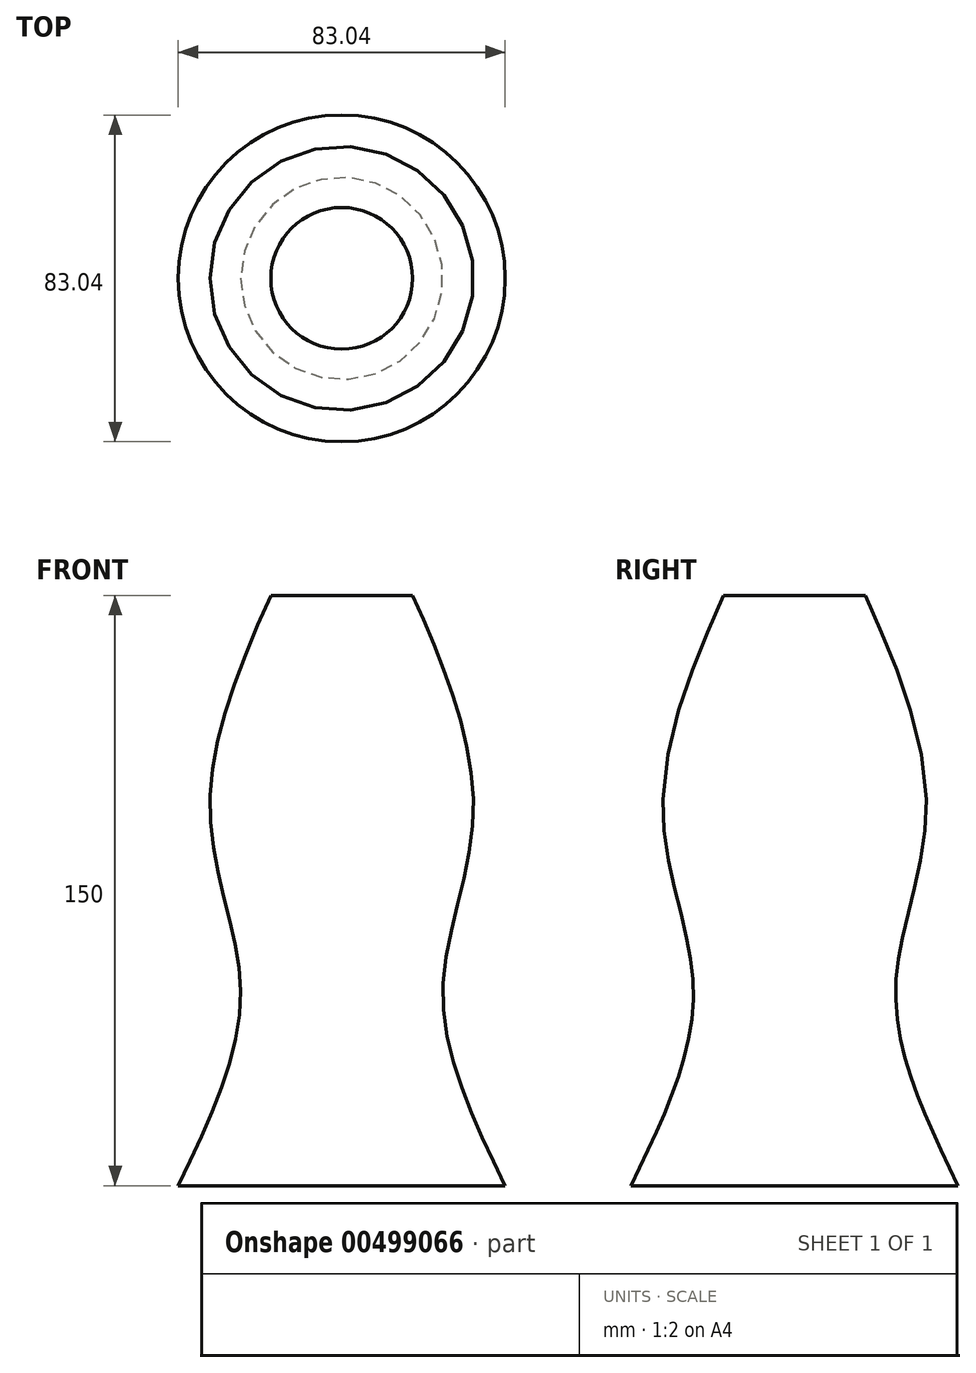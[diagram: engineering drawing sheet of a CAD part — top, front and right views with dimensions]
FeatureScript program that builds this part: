
annotation { "Feature Type Name" : "Feature", "Feature Type Description" : "" }
export const myFeature = defineFeature(function(context is Context, id is Id, definition is map)
    precondition{}
    {
        {
            var Q0;
            Q0=qCreatedBy(makeId("Front.planeOp"),FACE);
            var sketch = newSketch(context, id + "F0", { "sketchPlane" : qUnion([Q0])});
            skLineSegment(sketch, "E0", {"start": v(0, 0) * mm, "end": v(0, 150) * mm});
            skPoint(sketch, "E1.visualSharp", {"position": v(21.62, 122.87) * mm});
            skPoint(sketch, "E2.visualSharp", {"position": v(21.62, 34.71) * mm});
            skPoint(sketch, "E3.visualSharp", {"position": v(53.93, 0) * mm});
            skLineSegment(sketch, "E4", {"start": v(0, 0) * mm, "end": v(41.52, 0) * mm});
            skFitSpline(sketch, "E5", {"points": [v(41.52, 0) * mm, v(25.68, 49) * mm, v(33.49, 96.25) * mm, v(10.89, 165.28) * mm], "startDerivative": vector(-75.4, 156.2) * mm, "endDerivative": vector(-90.35, 191.6) * mm});
            skLineSegment(sketch, "E6", {"start": v(0, 150) * mm, "end": v(18, 150) * mm});
            skSolve(sketch);
        }
        {
            var Q0;
            Q0=qSketchRegion(id+"F0",true);
            var Q1;
            Q1=sQuery(id+"F0.wireOp",EDGE,"E0");
            revolve(context, id + "F1", {"surfaceOperationType" : NewSurfaceOperationType.NEW, "entities" : qUnion([Q0]), "axis" : qUnion([Q1]), "revolveType" : RevolveType.FULL});
        }
    });
